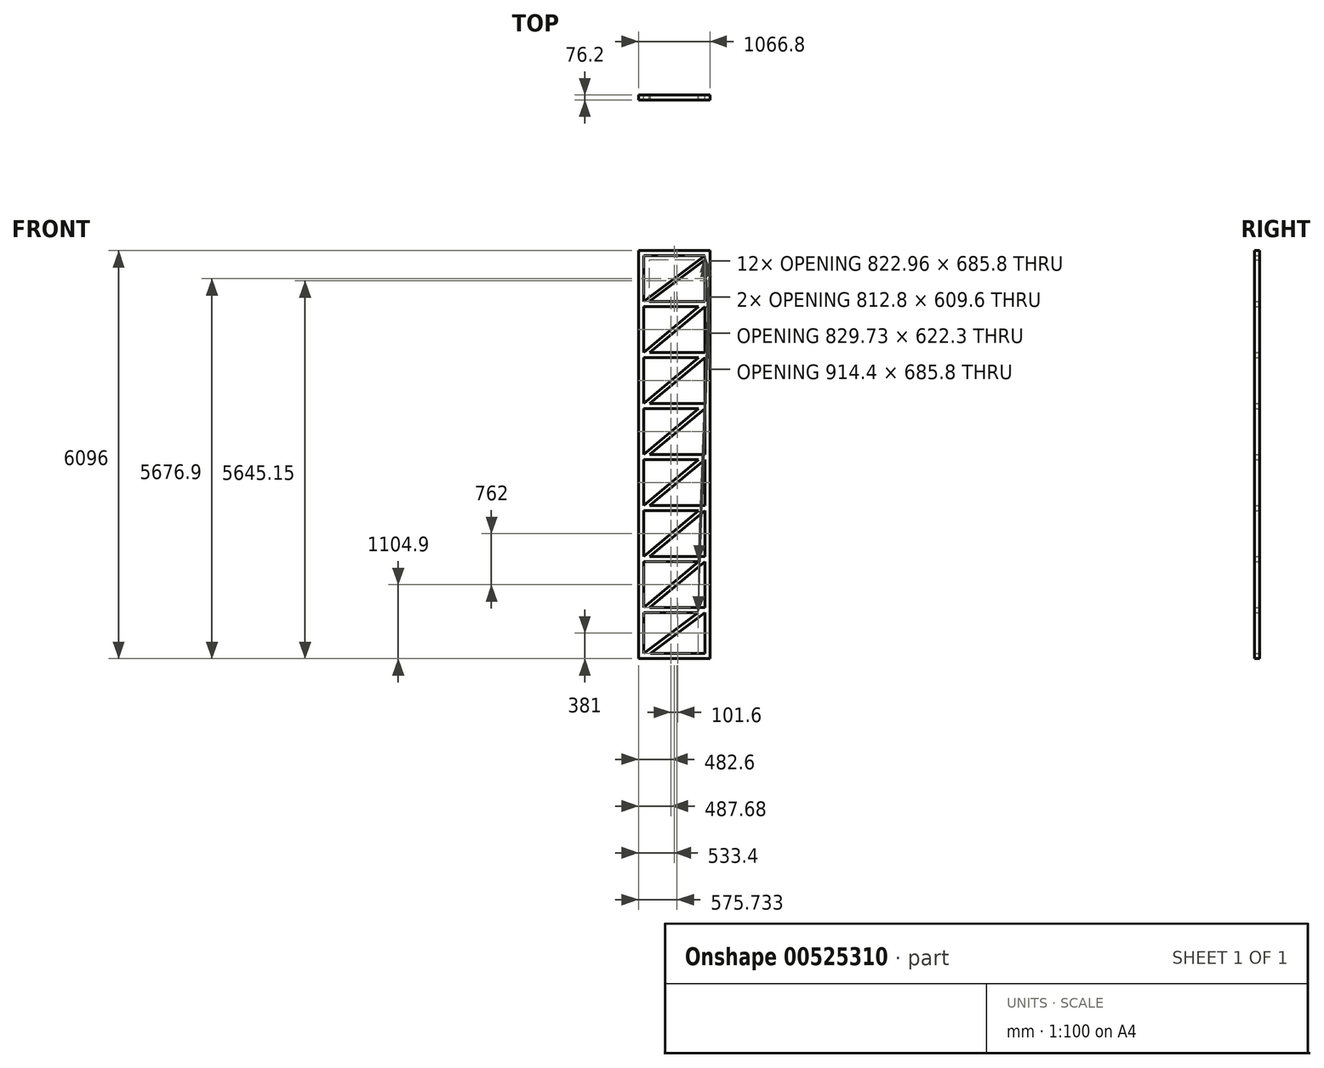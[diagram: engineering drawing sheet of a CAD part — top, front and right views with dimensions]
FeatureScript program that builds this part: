
annotation { "Feature Type Name" : "Feature", "Feature Type Description" : "" }
export const myFeature = defineFeature(function(context is Context, id is Id, definition is map)
    precondition{}
    {
        {
            var Q0;
            Q0=qCreatedBy(makeId("Front.planeOp"),FACE);
            var sketch = newSketch(context, id + "F0", { "sketchPlane" : qUnion([Q0])});
            skLineSegment(sketch, "E0.bottom", {"start": v(0, 0) * mm, "end": v(1066.8, 0) * mm});
            skLineSegment(sketch, "E0.top", {"start": v(0, 6096) * mm, "end": v(1066.8, 6096) * mm});
            skLineSegment(sketch, "E0.left", {"start": v(0, 0) * mm, "end": v(0, 6096) * mm});
            skLineSegment(sketch, "E0.right", {"start": v(1066.8, 0) * mm, "end": v(1066.8, 6096) * mm});
            skLineSegment(sketch, "E1.bottom", {"start": v(177.8, 76.2) * mm, "end": v(990.6, 76.2) * mm});
            skLineSegment(sketch, "E1.top", {"start": v(76.2, 6019.8) * mm, "end": v(990.6, 6019.8) * mm});
            skLineSegment(sketch, "E1.left", {"start": v(76.2, 76.2) * mm, "end": v(76.2, 685.8) * mm});
            skLineSegment(sketch, "E1.right", {"start": v(990.6, 76.2) * mm, "end": v(990.6, 685.8) * mm});
            skLineSegment(sketch, "E2", {"start": v(76.2, 76.2) * mm, "end": v(889, 685.8) * mm});
            skLineSegment(sketch, "E3", {"start": v(990.6, 762) * mm, "end": v(167.64, 762) * mm});
            skLineSegment(sketch, "E4", {"start": v(76.2, 762) * mm, "end": v(899.16, 1447.8) * mm});
            skLineSegment(sketch, "E5", {"start": v(990.6, 1524) * mm, "end": v(167.64, 1524) * mm});
            skLineSegment(sketch, "E6", {"start": v(76.2, 1524) * mm, "end": v(899.16, 2209.8) * mm});
            skLineSegment(sketch, "E7", {"start": v(990.6, 2286) * mm, "end": v(167.64, 2286) * mm});
            skLineSegment(sketch, "E8", {"start": v(76.2, 2286) * mm, "end": v(899.16, 2971.8) * mm});
            skLineSegment(sketch, "E9", {"start": v(990.6, 3048) * mm, "end": v(167.64, 3048) * mm});
            skLineSegment(sketch, "E10", {"start": v(76.2, 3048) * mm, "end": v(899.16, 3733.8) * mm});
            skLineSegment(sketch, "E11", {"start": v(990.6, 3810) * mm, "end": v(167.64, 3810) * mm});
            skLineSegment(sketch, "E12", {"start": v(76.2, 3810) * mm, "end": v(899.16, 4495.8) * mm});
            skLineSegment(sketch, "E13", {"start": v(990.6, 4572) * mm, "end": v(167.64, 4572) * mm});
            skLineSegment(sketch, "E14", {"start": v(76.2, 4572) * mm, "end": v(899.16, 5257.8) * mm});
            skLineSegment(sketch, "E15", {"start": v(990.6, 5334) * mm, "end": v(160.87, 5334) * mm});
            skLineSegment(sketch, "E16", {"start": v(76.2, 5334) * mm, "end": v(990.6, 6019.8) * mm});
            skLineSegment(sketch, "E17", {"start": v(160.87, 5334) * mm, "end": v(990.6, 5956.3) * mm});
            skLineSegment(sketch, "E18", {"start": v(76.2, 5257.8) * mm, "end": v(899.16, 5257.8) * mm});
            skLineSegment(sketch, "E19", {"start": v(990.6, 5257.8) * mm, "end": v(167.64, 4572) * mm});
            skLineSegment(sketch, "E20", {"start": v(76.2, 4495.8) * mm, "end": v(899.16, 4495.8) * mm});
            skLineSegment(sketch, "E21", {"start": v(990.6, 4495.8) * mm, "end": v(167.64, 3810) * mm});
            skLineSegment(sketch, "E22", {"start": v(76.2, 3733.8) * mm, "end": v(899.16, 3733.8) * mm});
            skLineSegment(sketch, "E23", {"start": v(990.6, 3733.8) * mm, "end": v(167.64, 3048) * mm});
            skLineSegment(sketch, "E24", {"start": v(76.2, 2971.8) * mm, "end": v(899.16, 2971.8) * mm});
            skLineSegment(sketch, "E25", {"start": v(990.6, 2971.8) * mm, "end": v(167.64, 2286) * mm});
            skLineSegment(sketch, "E26", {"start": v(76.2, 2209.8) * mm, "end": v(899.16, 2209.8) * mm});
            skLineSegment(sketch, "E27", {"start": v(990.6, 2209.8) * mm, "end": v(167.64, 1524) * mm});
            skLineSegment(sketch, "E28", {"start": v(76.2, 1447.8) * mm, "end": v(899.16, 1447.8) * mm});
            skLineSegment(sketch, "E29", {"start": v(990.6, 1447.8) * mm, "end": v(167.64, 762) * mm});
            skLineSegment(sketch, "E30", {"start": v(76.2, 685.8) * mm, "end": v(889, 685.8) * mm});
            skLineSegment(sketch, "E31", {"start": v(990.6, 685.8) * mm, "end": v(177.8, 76.2) * mm});
            skLineSegment(sketch, "E32.trimOffspring", {"start": v(76.2, 5334) * mm, "end": v(76.2, 6019.8) * mm});
            skLineSegment(sketch, "E33.trimOffspring", {"start": v(990.6, 5334) * mm, "end": v(990.6, 5956.3) * mm});
            skLineSegment(sketch, "E34.trimOffspring", {"start": v(76.2, 4572) * mm, "end": v(76.2, 5257.8) * mm});
            skLineSegment(sketch, "E35.trimOffspring", {"start": v(990.6, 4572) * mm, "end": v(990.6, 5257.8) * mm});
            skLineSegment(sketch, "E36.trimOffspring", {"start": v(76.2, 3810) * mm, "end": v(76.2, 4495.8) * mm});
            skLineSegment(sketch, "E37.trimOffspring", {"start": v(990.6, 3810) * mm, "end": v(990.6, 4495.8) * mm});
            skLineSegment(sketch, "E38.trimOffspring", {"start": v(76.2, 3048) * mm, "end": v(76.2, 3733.8) * mm});
            skLineSegment(sketch, "E39.trimOffspring", {"start": v(990.6, 3048) * mm, "end": v(990.6, 3733.8) * mm});
            skLineSegment(sketch, "E40.trimOffspring", {"start": v(76.2, 2286) * mm, "end": v(76.2, 2971.8) * mm});
            skLineSegment(sketch, "E41.trimOffspring", {"start": v(990.6, 2286) * mm, "end": v(990.6, 2971.8) * mm});
            skLineSegment(sketch, "E42.trimOffspring", {"start": v(76.2, 1524) * mm, "end": v(76.2, 2209.8) * mm});
            skLineSegment(sketch, "E43.trimOffspring", {"start": v(990.6, 1524) * mm, "end": v(990.6, 2209.8) * mm});
            skLineSegment(sketch, "E44.trimOffspring", {"start": v(76.2, 762) * mm, "end": v(76.2, 1447.8) * mm});
            skLineSegment(sketch, "E45.trimOffspring", {"start": v(990.6, 762) * mm, "end": v(990.6, 1447.8) * mm});
            skSolve(sketch);
        }
        {
            var Q0;
            Q0=makeQuery(id+"F0.imprint","IMPRINT",FACE,{"disambiguationData":[TD([[makeQuery(id+"F0.imprint","IMPRINT",EDGE,{"derivedFrom":sQuery(id+"F0.wireOp",EDGE,"E0.bottom")}),1.0]])]});
            extrude(context, id + "F1", {"entities" : qUnion([Q0]), "depth" : 76.2 * mm, "offsetDistance" : 25.4 * mm});
        }
    });
